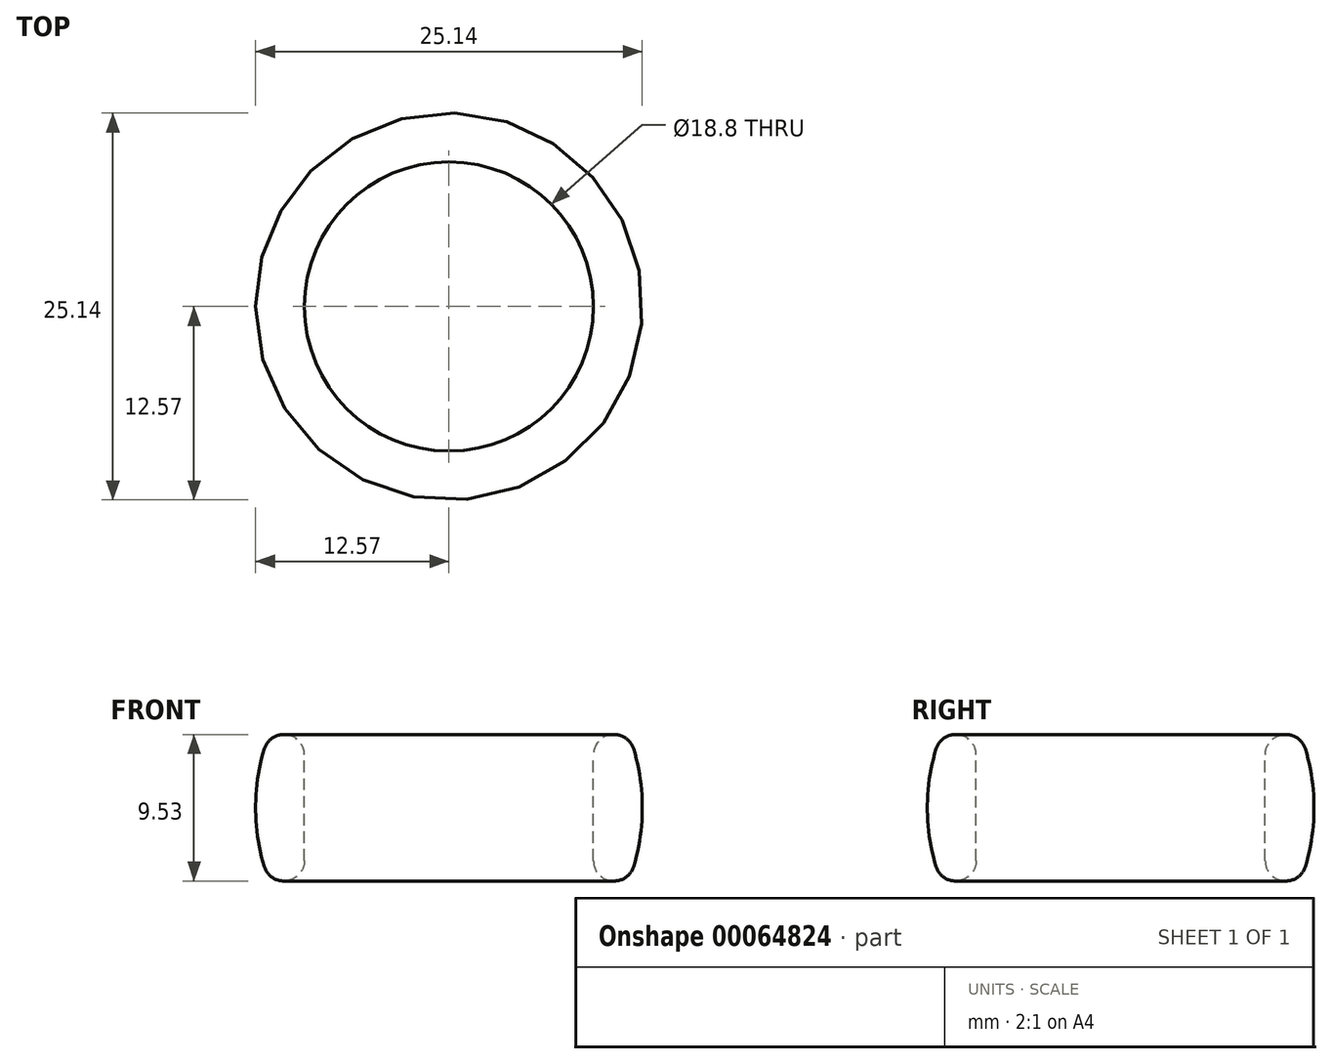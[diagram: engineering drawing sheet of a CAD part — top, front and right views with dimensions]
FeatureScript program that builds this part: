
annotation { "Feature Type Name" : "Feature", "Feature Type Description" : "" }
export const myFeature = defineFeature(function(context is Context, id is Id, definition is map)
    precondition{}
    {
        {
            var Q0;
            Q0=qCreatedBy(makeId("Front.planeOp"),FACE);
            var sketch = newSketch(context, id + "F0", { "sketchPlane" : qUnion([Q0])});
            skArc(sketch, "E0", {"start": v(11.69, 0) * mm, "mid": v(12.57, 4.76) * mm, "end": v(11.69, 9.53) * mm});
            skLineSegment(sketch, "E1", {"start": v(9.4, 9.53) * mm, "end": v(11.69, 9.53) * mm});
            skLineSegment(sketch, "E2", {"start": v(9.4, 0) * mm, "end": v(11.69, 0) * mm});
            skLineSegment(sketch, "E3", {"start": v(9.4, 9.52) * mm, "end": v(0, 9.52) * mm, "construction": true});
            skLineSegment(sketch, "E4", {"start": v(0, 9.52) * mm, "end": v(0, 0) * mm, "construction": true});
            skLineSegment(sketch, "E5", {"start": v(0, 0) * mm, "end": v(9.4, 0) * mm, "construction": true});
            skLineSegment(sketch, "E6", {"start": v(9.4, 0) * mm, "end": v(9.4, 9.53) * mm});
            skSolve(sketch);
        }
        {
            var Q0;
            Q0 = qSketchRegion(id + "F0", true);
            var Q1;
            Q1=sQuery(id+"F0.wireOp",EDGE,"E4");
            revolve(context, id + "F1", {"entities" : qUnion([Q0]), "axis" : qUnion([Q1]), "revolveType" : RevolveType.FULL});
        }
        {
            var Q0;
            Q0=makeQuery(id+"F1.opRevolve","SWEPT_EDGE",EDGE,{"disambiguationData":[OSD([sQuery(id+"F0.wireOp",EDGE,"E0"),sQuery(id+"F0.wireOp",EDGE,"E1")])]});
            var Q1;
            Q1=makeQuery(id+"F1.opRevolve","SWEPT_EDGE",EDGE,{"disambiguationData":[OSD([sQuery(id+"F0.wireOp",EDGE,"aN8Ml5RG-UJdO-SGzw-ZjNv-5UMk1wiNXroe"),sQuery(id+"F0.wireOp",EDGE,"E1")])]});
            var Q2;
            Q2=makeQuery(id+"F1.opRevolve","SWEPT_EDGE",EDGE,{"disambiguationData":[OSD([sQuery(id+"F0.wireOp",EDGE,"E0"),sQuery(id+"F0.wireOp",EDGE,"E2")])]});
            var Q3;
            Q3=makeQuery(id+"F1.opRevolve","SWEPT_EDGE",EDGE,{"disambiguationData":[OSD([sQuery(id+"F0.wireOp",EDGE,"aN8Ml5RG-UJdO-SGzw-ZjNv-5UMk1wiNXroe"),sQuery(id+"F0.wireOp",EDGE,"E2")])]});
            fillet(context, id + "F2", {"entities" : qUnion([Q0, Q1, Q2, Q3]), "radius" : 1.32 * mm, "tangentPropagation" : true, "allowEdgeOverflow" : false});
        }
    });
